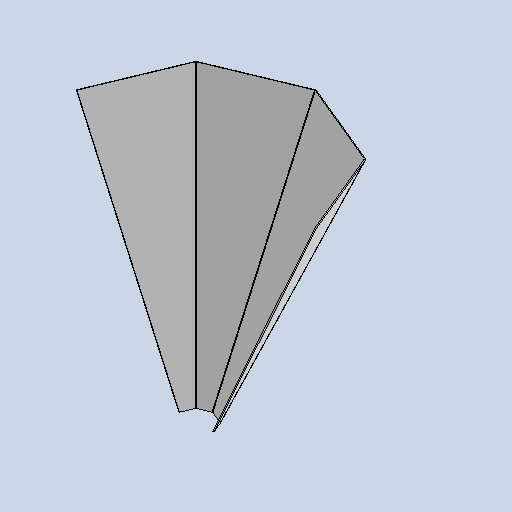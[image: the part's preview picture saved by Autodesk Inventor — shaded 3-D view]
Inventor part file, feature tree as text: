
AUTODESK INVENTOR PART (.ipt)
format: ipt  version: 2025.1 (Build 291241020, 241B)  size: 235,008 bytes
history: native  units: mm
features: sketch x2, plane x1, loft x1, sheet_metal_op x1, other x1
ambient origin geometry x8: Origin, YZ Plane, XZ Plane, XY Plane, X Axis, Y Axis, Z Axis, Center Point
bodies: Body1 (feature_tree)
feature tree (6):
  sketch  "Sketch15"  dims[d116=24.0mm d117=430.0mm]
  plane  "Work Plane1"
  loft  "Lofted Flange1"
  sketch  "Sketch16"  dims[d118=450.0mm d119=2.0mm d120=0.5mm d121=2.0mm d122=2.0mm d123=1.0mm d124=4.0mm d125=2.0mm]
  sheet_metal_op  "Bend1"
  other  "Definition1"
